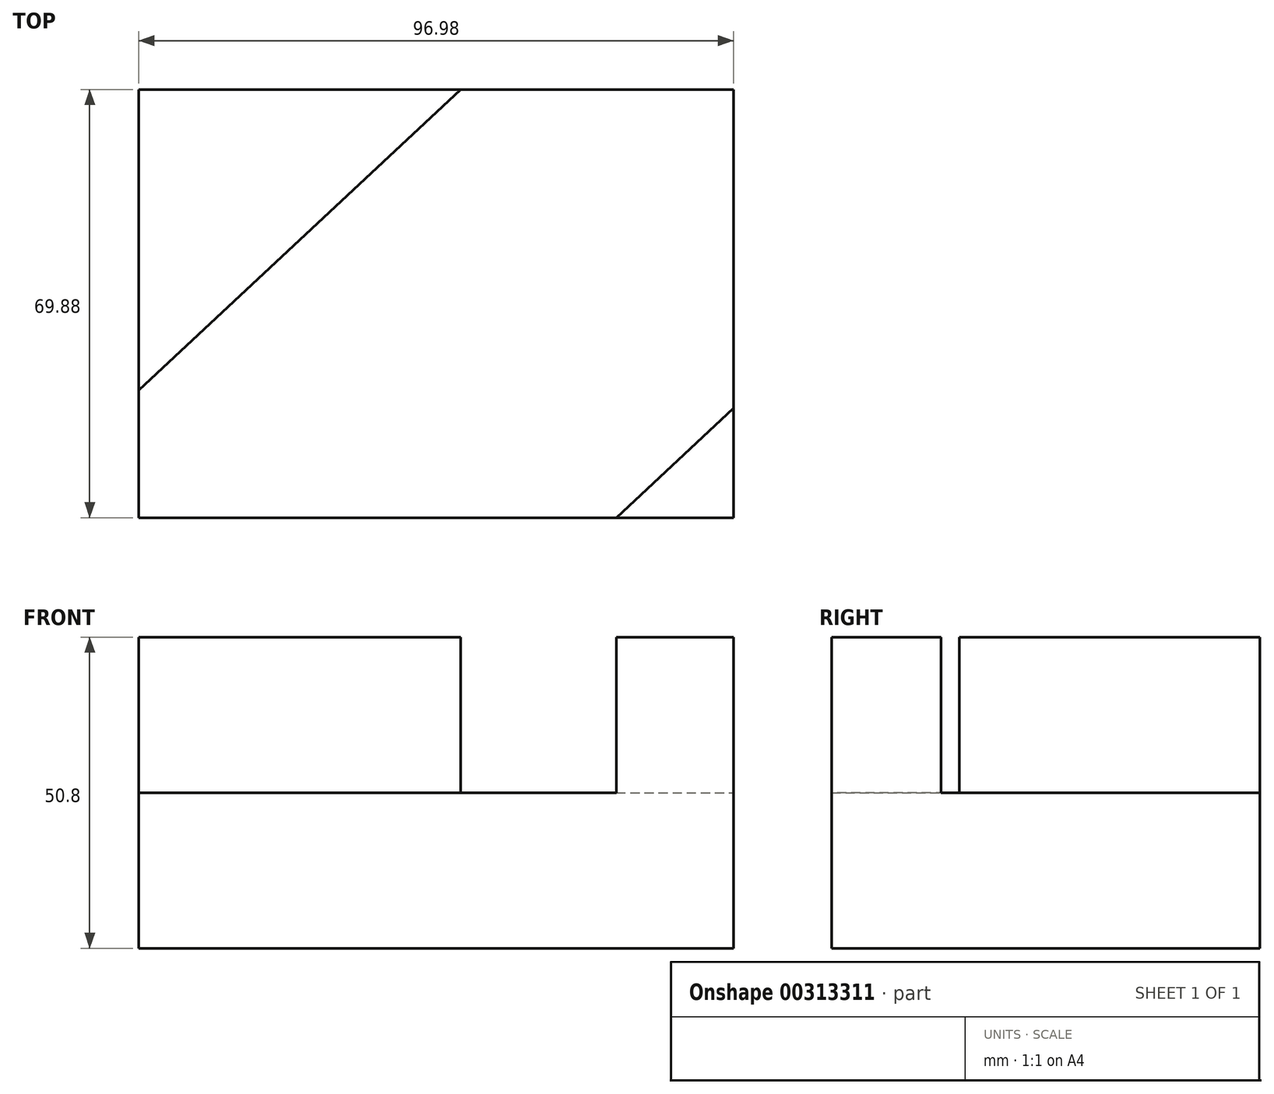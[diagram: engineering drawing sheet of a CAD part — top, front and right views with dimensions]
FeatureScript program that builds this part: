
annotation { "Feature Type Name" : "Feature", "Feature Type Description" : "" }
export const myFeature = defineFeature(function(context is Context, id is Id, definition is map)
    precondition{}
    {
        {
            var Q0;
            Q0=qCreatedBy(makeId("Top.planeOp"),FACE);
            var sketch = newSketch(context, id + "F0", { "sketchPlane" : qUnion([Q0])});
            skLineSegment(sketch, "E0", {"start": v(-44.78, 42.64) * mm, "end": v(-44.78, -27.24) * mm});
            skLineSegment(sketch, "E1", {"start": v(-44.78, -27.24) * mm, "end": v(52.2, -27.24) * mm});
            skLineSegment(sketch, "E2", {"start": v(52.2, -27.24) * mm, "end": v(52.2, 42.64) * mm});
            skLineSegment(sketch, "E3", {"start": v(52.2, 42.64) * mm, "end": v(-44.78, 42.64) * mm});
            skSolve(sketch);
        }
        {
            var Q0;
            Q0=makeQuery(id+"F0.imprint","IMPRINT",FACE,{"disambiguationData":[TD([[makeQuery(id+"F0.imprint","IMPRINT",EDGE,{"derivedFrom":sQuery(id+"F0.wireOp",EDGE,"E0")}),1.0]])]});
            extrude(context, id + "F1", {"entities" : qUnion([Q0]), "depth" : 25.4 * mm});
        }
        {
            var Q0;
            Q0=makeQuery(id+"F1.opExtrude","CAP_FACE",FACE,{"disambiguationData":[OSD([sQuery(id+"F0.wireOp",EDGE,"E0"),sQuery(id+"F0.wireOp",EDGE,"E1"),sQuery(id+"F0.wireOp",EDGE,"E2"),sQuery(id+"F0.wireOp",EDGE,"E3")])],"isStart":false});
            var sketch = newSketch(context, id + "F2", { "sketchPlane" : qUnion([Q0])});
            skLineSegment(sketch, "E4", {"start": v(-44.78, -6.42) * mm, "end": v(7.7, 42.64) * mm});
            skLineSegment(sketch, "E5", {"start": v(7.7, 42.64) * mm, "end": v(-44.78, 42.64) * mm});
            skLineSegment(sketch, "E6", {"start": v(-44.78, 42.64) * mm, "end": v(-44.78, -6.42) * mm});
            skLineSegment(sketch, "E7", {"start": v(33.09, -27.24) * mm, "end": v(52.2, -9.38) * mm});
            skSolve(sketch);
        }
        {
            var Q0;
            Q0=makeQuery(id+"F2.imprint","IMPRINT",FACE,{"disambiguationData":[TD([[makeQuery(id+"F2.imprint","IMPRINT",EDGE,{"derivedFrom":sQuery(id+"F2.wireOp",EDGE,"E4")}),1.0]])]});
            var Q1;
            {var subQ0=sQuery(id+"F2.wireOp",EDGE,"E7");Q1=makeQuery(id+"F2.imprint","IMPRINT",FACE,{"disambiguationData":[TD([[makeQuery(id+"F2.imprint","IMPRINT",EDGE,{"derivedFrom":subQ0}),-1.0]])]});}
            extrude(context, id + "F3", {"entities" : qUnion([Q0, Q1]), "operationType" : NewBodyOperationType.ADD, "depth" : 25.4 * mm});
        }
    });
